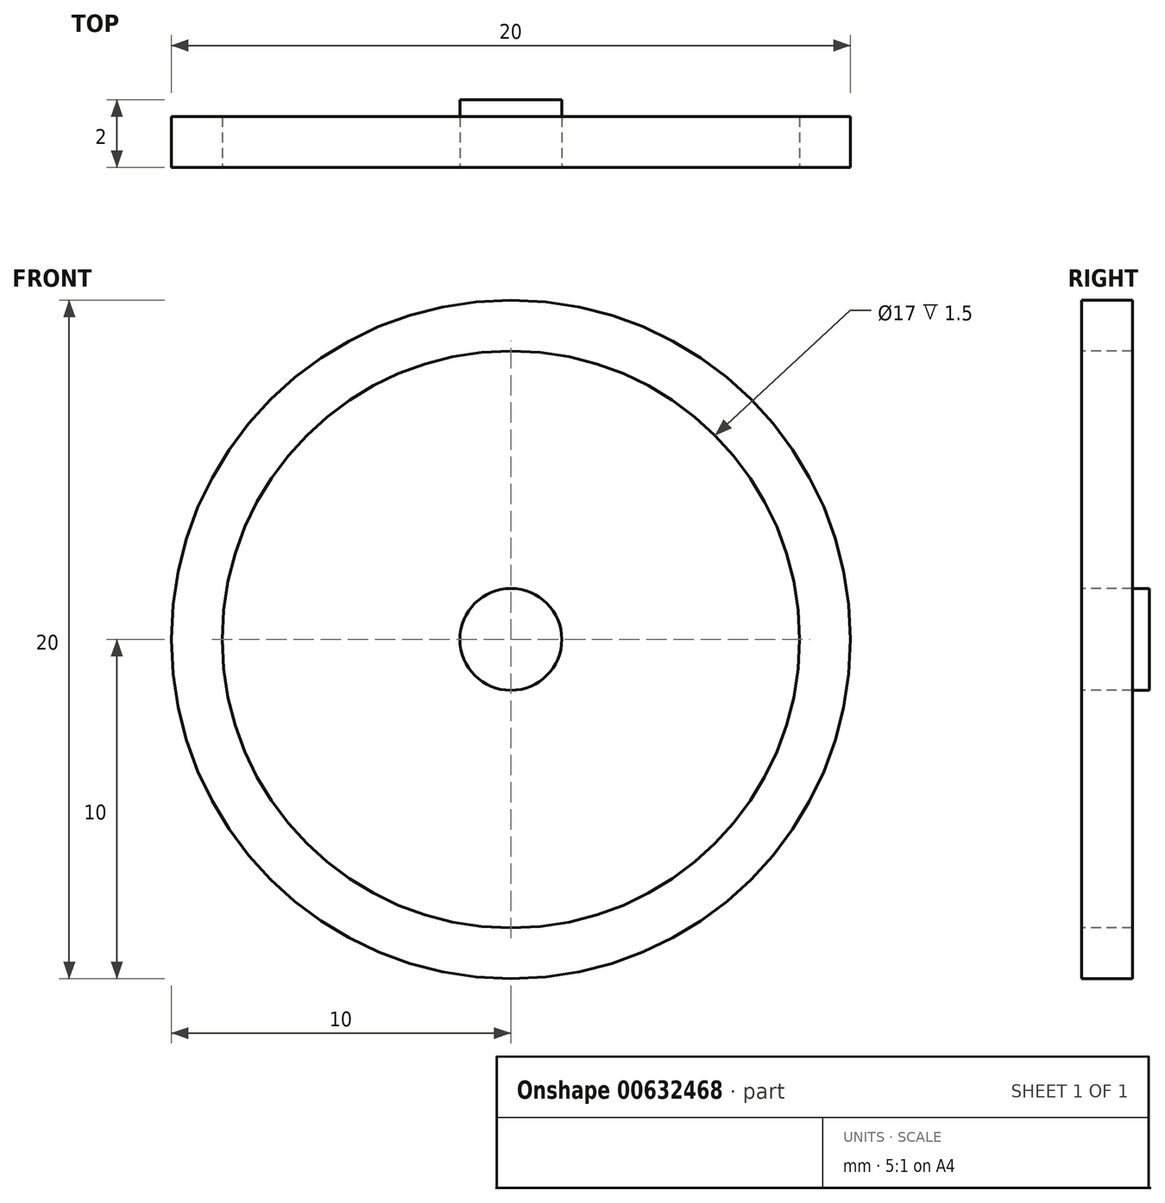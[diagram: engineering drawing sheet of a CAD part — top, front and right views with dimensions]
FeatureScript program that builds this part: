
annotation { "Feature Type Name" : "Feature", "Feature Type Description" : "" }
export const myFeature = defineFeature(function(context is Context, id is Id, definition is map)
    precondition{}
    {
        {
            var Q0;
            Q0=qCreatedBy(makeId("Right.planeOp"),FACE);
            var sketch = newSketch(context, id + "F0", { "sketchPlane" : qUnion([Q0])});
            skLineSegment(sketch, "E0.bottom", {"start": v(0, 0) * mm, "end": v(2, 0) * mm});
            skLineSegment(sketch, "E0.top", {"start": v(0, 1.5) * mm, "end": v(2, 1.5) * mm});
            skLineSegment(sketch, "E0.left", {"start": v(0, 0) * mm, "end": v(0, 1.5) * mm});
            skLineSegment(sketch, "E0.right", {"start": v(2, 0) * mm, "end": v(2, 1.5) * mm});
            skLineSegment(sketch, "E1.bottom", {"start": v(0, 1.5) * mm, "end": v(1, 1.5) * mm});
            skLineSegment(sketch, "E1.top", {"start": v(0, 8.5) * mm, "end": v(1, 8.5) * mm});
            skLineSegment(sketch, "E1.left", {"start": v(0, 1.5) * mm, "end": v(0, 8.5) * mm});
            skLineSegment(sketch, "E1.right", {"start": v(1, 1.5) * mm, "end": v(1, 8.5) * mm});
            skLineSegment(sketch, "E2.bottom", {"start": v(0, 8.5) * mm, "end": v(1.5, 8.5) * mm});
            skLineSegment(sketch, "E2.top", {"start": v(0, 10) * mm, "end": v(1.5, 10) * mm});
            skLineSegment(sketch, "E2.left", {"start": v(0, 8.5) * mm, "end": v(0, 10) * mm});
            skLineSegment(sketch, "E2.right", {"start": v(1.5, 8.5) * mm, "end": v(1.5, 10) * mm});
            skSolve(sketch);
        }
        {
            var Q0;
            Q0=makeQuery(id+"F0.imprint","IMPRINT",FACE,{"disambiguationData":[TD([[makeQuery(id+"F0.imprint","IMPRINT",EDGE,{"derivedFrom":sQuery(id+"F0.wireOp",EDGE,"E2.top")}),-1.0]])]});
            var Q1;
            Q1=makeQuery(id+"F0.imprint","IMPRINT",FACE,{"disambiguationData":[TD([[makeQuery(id+"F0.imprint","IMPRINT",EDGE,{"derivedFrom":sQuery(id+"F0.wireOp",EDGE,"E1.bottom")}),1.0]])]});
            var Q2;
            Q2=makeQuery(id+"F0.imprint","IMPRINT",FACE,{"disambiguationData":[TD([[makeQuery(id+"F0.imprint","IMPRINT",EDGE,{"derivedFrom":sQuery(id+"F0.wireOp",EDGE,"E0.bottom")}),1.0]])]});
            var Q3;
            Q3=sQuery(id+"F0.wireOp",EDGE,"E0.bottom");
            revolve(context, id + "F1", {"entities" : qUnion([Q0, Q1, Q2]), "axis" : qUnion([Q3]), "revolveType" : RevolveType.FULL});
        }
    });
